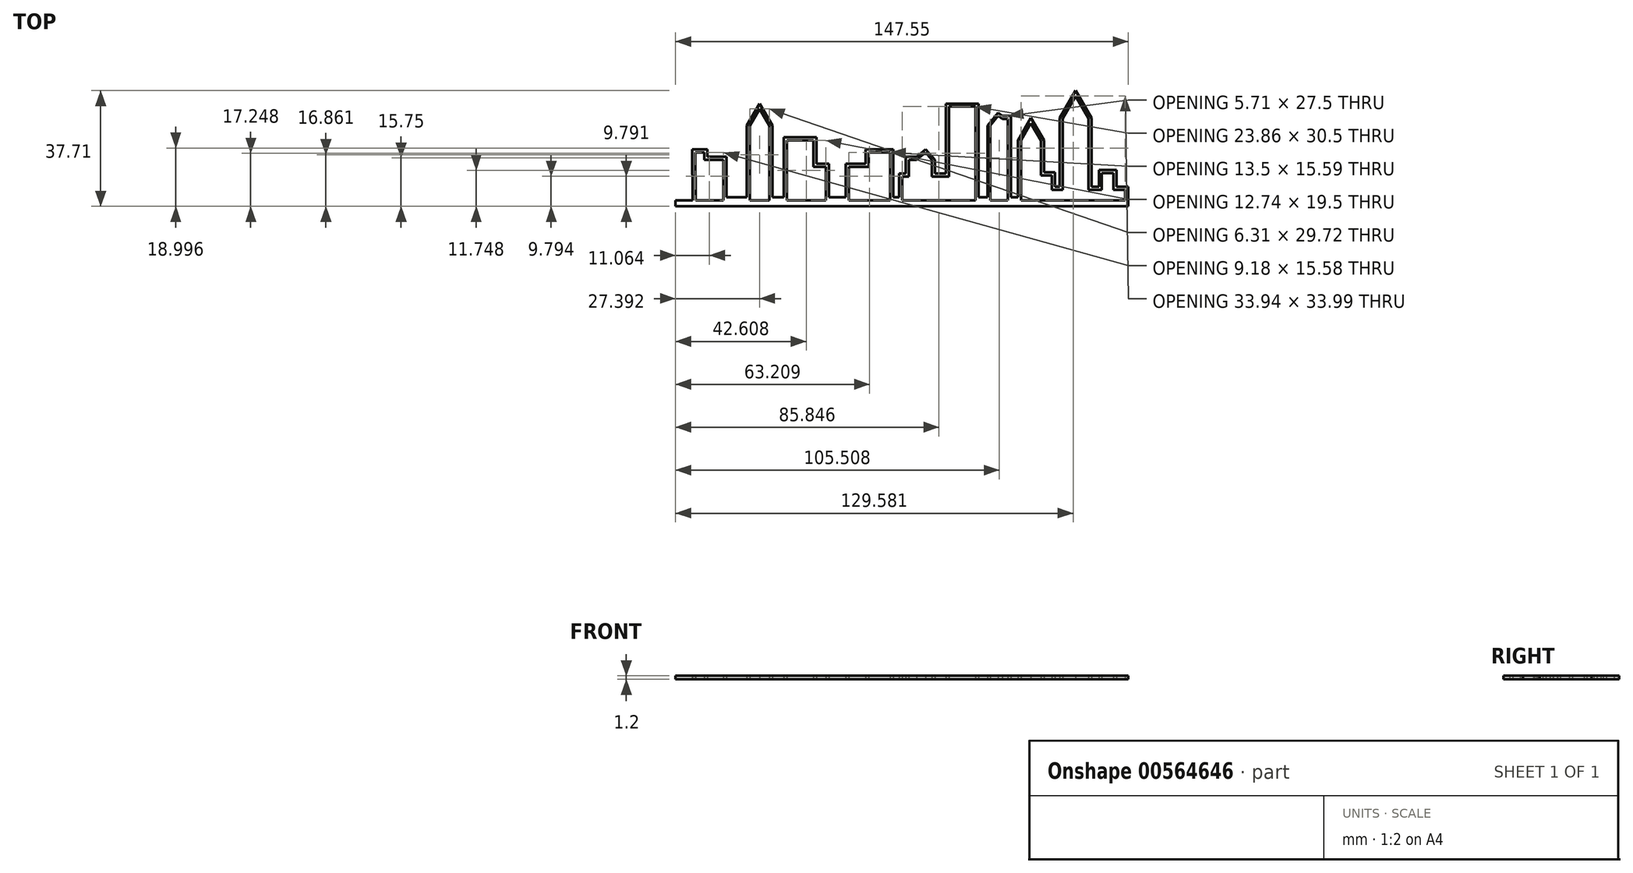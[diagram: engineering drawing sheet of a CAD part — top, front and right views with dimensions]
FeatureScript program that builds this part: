
annotation { "Feature Type Name" : "Feature", "Feature Type Description" : "" }
export const myFeature = defineFeature(function(context is Context, id is Id, definition is map)
    precondition{}
    {
        {
            var Q0;
            Q0=qCreatedBy(makeId("Top.planeOp"),FACE);
            var sketch = newSketch(context, id + "F0", { "sketchPlane" : qUnion([Q0])});
            skLineSegment(sketch, "E0", {"start": v(-8.8, 15.59) * mm, "end": v(-8.8, 10.82) * mm});
            skLineSegment(sketch, "E1", {"start": v(-8.8, 10.82) * mm, "end": v(-15.3, 10.82) * mm});
            skLineSegment(sketch, "E2", {"start": v(-15.3, 10.82) * mm, "end": v(-15.3, 1) * mm});
            skLineSegment(sketch, "E3", {"start": v(-17.9, 0) * mm, "end": v(-22.77, 0) * mm});
            skLineSegment(sketch, "E4", {"start": v(-22.77, 0) * mm, "end": v(-22.77, 10.82) * mm});
            skLineSegment(sketch, "E5", {"start": v(-26.82, 10.82) * mm, "end": v(-22.77, 10.82) * mm});
            skLineSegment(sketch, "E6", {"start": v(-26.82, 10.82) * mm, "end": v(-26.82, 19.5) * mm});
            skLineSegment(sketch, "E7", {"start": v(-26.82, 19.5) * mm, "end": v(-35.51, 19.5) * mm});
            skLineSegment(sketch, "E8", {"start": v(-35.51, 19.5) * mm, "end": v(-35.51, 0) * mm});
            skLineSegment(sketch, "E9", {"start": v(-35.51, 0) * mm, "end": v(-41.2, 0) * mm});
            skLineSegment(sketch, "E10", {"start": v(-41.2, 0) * mm, "end": v(-41.2, 24.26) * mm});
            skLineSegment(sketch, "E11", {"start": v(-41.2, 24.26) * mm, "end": v(-44.36, 29.72) * mm});
            skLineSegment(sketch, "E12", {"start": v(-47.51, 0) * mm, "end": v(-51.85, 0) * mm});
            skLineSegment(sketch, "E13", {"start": v(0, 0) * mm, "end": v(2.17, 0) * mm});
            skLineSegment(sketch, "E14", {"start": v(2.17, 0) * mm, "end": v(2.17, 7.73) * mm});
            skLineSegment(sketch, "E15", {"start": v(2.17, 7.73) * mm, "end": v(4.34, 7.73) * mm});
            skLineSegment(sketch, "E16", {"start": v(4.34, 7.73) * mm, "end": v(4.34, 13.15) * mm});
            skLineSegment(sketch, "E17", {"start": v(4.34, 13.15) * mm, "end": v(6.78, 13.15) * mm});
            skLineSegment(sketch, "E18", {"start": v(6.78, 13.15) * mm, "end": v(9.76, 15.59) * mm});
            skLineSegment(sketch, "E19", {"start": v(9.76, 15.59) * mm, "end": v(11.76, 13.15) * mm});
            skLineSegment(sketch, "E20", {"start": v(11.76, 13.15) * mm, "end": v(11.76, 7.73) * mm});
            skLineSegment(sketch, "E21", {"start": v(11.76, 7.73) * mm, "end": v(17.35, 7.73) * mm});
            skLineSegment(sketch, "E22", {"start": v(17.35, 7.73) * mm, "end": v(17.35, 30.5) * mm});
            skLineSegment(sketch, "E23", {"start": v(17.35, 30.5) * mm, "end": v(26.02, 30.5) * mm});
            skLineSegment(sketch, "E24", {"start": v(26.02, 30.5) * mm, "end": v(26.02, 7.73) * mm});
            skLineSegment(sketch, "E25", {"start": v(26.02, 7.73) * mm, "end": v(26.02, 0) * mm});
            skLineSegment(sketch, "E26", {"start": v(26.02, 0) * mm, "end": v(30.9, 0) * mm});
            skLineSegment(sketch, "E27", {"start": v(30.9, 0) * mm, "end": v(30.9, 19.5) * mm});
            skLineSegment(sketch, "E28", {"start": v(30.9, 19.5) * mm, "end": v(30.9, 24.26) * mm});
            skLineSegment(sketch, "E29", {"start": v(30.9, 24.26) * mm, "end": v(33.42, 27.5) * mm});
            skLineSegment(sketch, "E30", {"start": v(33.42, 27.5) * mm, "end": v(34.76, 26.45) * mm});
            skLineSegment(sketch, "E31", {"start": v(34.76, 26.45) * mm, "end": v(36.61, 26.45) * mm});
            skLineSegment(sketch, "E32", {"start": v(36.61, 26.45) * mm, "end": v(36.61, 24.26) * mm});
            skLineSegment(sketch, "E33", {"start": v(36.61, 24.26) * mm, "end": v(36.61, 0) * mm});
            skLineSegment(sketch, "E34", {"start": v(44.1, 25.12) * mm, "end": v(47.36, 19.5) * mm});
            skLineSegment(sketch, "E35", {"start": v(47.36, 19.5) * mm, "end": v(47.36, 8.1) * mm});
            skLineSegment(sketch, "E36", {"start": v(47.36, 8.1) * mm, "end": v(50.96, 8.1) * mm});
            skLineSegment(sketch, "E37", {"start": v(50.96, 8.1) * mm, "end": v(50.96, 3.39) * mm});
            skLineSegment(sketch, "E38", {"start": v(50.96, 3.39) * mm, "end": v(54.48, 3.39) * mm});
            skLineSegment(sketch, "E39", {"start": v(58.69, 34) * mm, "end": v(62.89, 26.71) * mm});
            skLineSegment(sketch, "E40", {"start": v(67.21, 3.39) * mm, "end": v(67.21, 8.81) * mm});
            skLineSegment(sketch, "E41", {"start": v(67.21, 8.81) * mm, "end": v(71, 8.81) * mm});
            skPoint(sketch, "E42.start.orphan", {"position": v(-66.14, 14.37) * mm});
            skLineSegment(sketch, "E43", {"start": v(-71.73, -2) * mm, "end": v(74.8, -2) * mm});
            skLineSegment(sketch, "E44", {"start": v(-66.14, 0) * mm, "end": v(74.8, 0) * mm});
            skLineSegment(sketch, "E45", {"start": v(74.8, 3.39) * mm, "end": v(74.8, 0) * mm});
            skPoint(sketch, "E46.orphan", {"position": v(76.22, -2) * mm});
            skLineSegment(sketch, "E47", {"start": v(74.8, -2) * mm, "end": v(75.8, -2) * mm});
            skLineSegment(sketch, "E48", {"start": v(75.8, -2) * mm, "end": v(75.8, 4.39) * mm});
            skPoint(sketch, "E49.start.orphan", {"position": v(72.9, 3.39) * mm});
            skLineSegment(sketch, "E50", {"start": v(74.8, 4.39) * mm, "end": v(72, 4.39) * mm});
            skLineSegment(sketch, "E51", {"start": v(72, 4.39) * mm, "end": v(72, 9.81) * mm});
            skLineSegment(sketch, "E52", {"start": v(68.57, 9.81) * mm, "end": v(72, 9.81) * mm});
            skLineSegment(sketch, "E53", {"start": v(74.8, 0) * mm, "end": v(75.8, 0) * mm});
            skLineSegment(sketch, "E54", {"start": v(66.21, 6.69) * mm, "end": v(66.21, 9.81) * mm});
            skLineSegment(sketch, "E55", {"start": v(68.57, 9.81) * mm, "end": v(66.21, 9.81) * mm});
            skLineSegment(sketch, "E56", {"start": v(66.21, 6.69) * mm, "end": v(66.21, 4.39) * mm});
            skLineSegment(sketch, "E57", {"start": v(64.7, 4.39) * mm, "end": v(66.21, 4.39) * mm});
            skLineSegment(sketch, "E58", {"start": v(64.7, 4.39) * mm, "end": v(63.88, 4.39) * mm});
            skLineSegment(sketch, "E59", {"start": v(54.48, 3.39) * mm, "end": v(54.48, 26.71) * mm});
            skLineSegment(sketch, "E60", {"start": v(53.48, 26.68) * mm, "end": v(53.48, 4.39) * mm});
            skLineSegment(sketch, "E61", {"start": v(53.48, 4.39) * mm, "end": v(51.96, 4.39) * mm});
            skLineSegment(sketch, "E62", {"start": v(51.96, 4.39) * mm, "end": v(51.96, 9.1) * mm});
            skLineSegment(sketch, "E63", {"start": v(51.96, 9.1) * mm, "end": v(48.36, 9.1) * mm});
            skPoint(sketch, "E64.start.orphan", {"position": v(39.32, 19.5) * mm});
            skLineSegment(sketch, "E65", {"start": v(54.48, 3.39) * mm, "end": v(74.8, 3.39) * mm});
            skLineSegment(sketch, "E66", {"start": v(71, 8.81) * mm, "end": v(71, 3.39) * mm});
            skPoint(sketch, "E67.orphan", {"position": v(71, 3.39) * mm});
            skPoint(sketch, "E68.orphan", {"position": v(74.8, 3.39) * mm});
            skPoint(sketch, "E69.end.orphan", {"position": v(62.88, 3.39) * mm});
            skLineSegment(sketch, "E70", {"start": v(62.89, 26.71) * mm, "end": v(62.89, 3.39) * mm});
            skLineSegment(sketch, "E71", {"start": v(62.89, 26.71) * mm, "end": v(54.48, 26.71) * mm});
            skLineSegment(sketch, "E72", {"start": v(54.48, 26.71) * mm, "end": v(58.69, 34) * mm});
            skLineSegment(sketch, "E73", {"start": v(63.89, 26.71) * mm, "end": v(63.88, 4.39) * mm});
            skLineSegment(sketch, "E74", {"start": v(63.89, 26.71) * mm, "end": v(58.7, 35.7) * mm});
            skLineSegment(sketch, "E75", {"start": v(53.48, 26.68) * mm, "end": v(58.7, 35.7) * mm});
            skLineSegment(sketch, "E76", {"start": v(48.36, 19.5) * mm, "end": v(48.36, 9.1) * mm});
            skLineSegment(sketch, "E77", {"start": v(48.36, 19.5) * mm, "end": v(44.1, 26.86) * mm});
            skLineSegment(sketch, "E78", {"start": v(37.61, 1) * mm, "end": v(37.61, 27.45) * mm});
            skLineSegment(sketch, "E79", {"start": v(34.76, 27.45) * mm, "end": v(37.61, 27.45) * mm});
            skLineSegment(sketch, "E80", {"start": v(34.23, 27.87) * mm, "end": v(34.41, 28.1) * mm});
            skLineSegment(sketch, "E81", {"start": v(34.76, 27.45) * mm, "end": v(33.42, 28.5) * mm});
            skLineSegment(sketch, "E82", {"start": v(33.42, 28.5) * mm, "end": v(29.9, 24.26) * mm});
            skLineSegment(sketch, "E83", {"start": v(29.9, 24.26) * mm, "end": v(29.9, 1) * mm});
            skPoint(sketch, "E84.start.orphan", {"position": v(28.46, 0) * mm});
            skLineSegment(sketch, "E85", {"start": v(29.9, 1) * mm, "end": v(27.02, 1) * mm});
            skLineSegment(sketch, "E86", {"start": v(27.02, 1) * mm, "end": v(27.02, 31.5) * mm});
            skPoint(sketch, "E87.start.orphan", {"position": v(21.69, 30.5) * mm});
            skLineSegment(sketch, "E88", {"start": v(27.02, 31.5) * mm, "end": v(16.35, 31.5) * mm});
            skLineSegment(sketch, "E89", {"start": v(16.35, 31.5) * mm, "end": v(16.35, 8.73) * mm});
            skPoint(sketch, "E90.start.orphan", {"position": v(14.55, 7.73) * mm});
            skLineSegment(sketch, "E91", {"start": v(16.35, 8.73) * mm, "end": v(12.76, 8.73) * mm});
            skLineSegment(sketch, "E92", {"start": v(12.76, 8.73) * mm, "end": v(12.76, 13.15) * mm});
            skLineSegment(sketch, "E93", {"start": v(4.34, 14.15) * mm, "end": v(6.78, 14.15) * mm});
            skLineSegment(sketch, "E94", {"start": v(6.78, 14.15) * mm, "end": v(9.76, 16.59) * mm});
            skLineSegment(sketch, "E95", {"start": v(12.76, 13.15) * mm, "end": v(9.76, 16.59) * mm});
            skLineSegment(sketch, "E96", {"start": v(4.34, 14.15) * mm, "end": v(3.34, 14.15) * mm});
            skLineSegment(sketch, "E97", {"start": v(3.34, 14.15) * mm, "end": v(3.34, 8.73) * mm});
            skLineSegment(sketch, "E98", {"start": v(-8.8, 15.59) * mm, "end": v(-1.8, 15.59) * mm});
            skLineSegment(sketch, "E99", {"start": v(-1.8, 15.59) * mm, "end": v(-1.8, 0) * mm});
            skLineSegment(sketch, "E100", {"start": v(3.34, 8.73) * mm, "end": v(1.17, 8.73) * mm});
            skLineSegment(sketch, "E101", {"start": v(1.17, 8.73) * mm, "end": v(1.17, 1) * mm});
            skLineSegment(sketch, "E102", {"start": v(1.17, 1) * mm, "end": v(-0.8, 1) * mm});
            skLineSegment(sketch, "E103", {"start": v(-0.8, 1) * mm, "end": v(-0.8, 16.59) * mm});
            skLineSegment(sketch, "E104", {"start": v(-0.8, 16.59) * mm, "end": v(-9.8, 16.59) * mm});
            skLineSegment(sketch, "E105", {"start": v(-9.8, 16.59) * mm, "end": v(-9.8, 11.82) * mm});
            skLineSegment(sketch, "E106", {"start": v(-9.8, 11.82) * mm, "end": v(-16.3, 11.82) * mm});
            skPoint(sketch, "E107.start.orphan", {"position": v(-20.33, 0) * mm});
            skLineSegment(sketch, "E108", {"start": v(-21.77, 1) * mm, "end": v(-21.77, 11.82) * mm});
            skLineSegment(sketch, "E109", {"start": v(-21.77, 11.82) * mm, "end": v(-25.82, 11.82) * mm});
            skLineSegment(sketch, "E110", {"start": v(-25.82, 11.82) * mm, "end": v(-25.82, 20.5) * mm});
            skLineSegment(sketch, "E111", {"start": v(-30.47, 20.5) * mm, "end": v(-25.82, 20.5) * mm});
            skLineSegment(sketch, "E112", {"start": v(-30.47, 20.5) * mm, "end": v(-36.51, 20.5) * mm});
            skPoint(sketch, "E113.start.orphan", {"position": v(-26.82, 15.16) * mm});
            skLineSegment(sketch, "E114", {"start": v(-36.51, 20.5) * mm, "end": v(-36.51, 1) * mm});
            skLineSegment(sketch, "E115", {"start": v(-36.51, 1) * mm, "end": v(-40.2, 1) * mm});
            skLineSegment(sketch, "E116", {"start": v(-40.2, 1) * mm, "end": v(-40.2, 24.26) * mm});
            skLineSegment(sketch, "E117", {"start": v(-41.2, 24.26) * mm, "end": v(-47.51, 24.26) * mm});
            skPoint(sketch, "E118.start.orphan", {"position": v(-47.51, 24.26) * mm});
            skPoint(sketch, "E119.end.orphan", {"position": v(-50.96, 1) * mm});
            skLineSegment(sketch, "E120", {"start": v(-47.51, 0) * mm, "end": v(-47.51, 24.26) * mm});
            skLineSegment(sketch, "E121", {"start": v(-47.51, 24.26) * mm, "end": v(-44.36, 29.72) * mm});
            skLineSegment(sketch, "E122", {"start": v(-48.51, 24.26) * mm, "end": v(-44.36, 31.45) * mm});
            skLineSegment(sketch, "E123", {"start": v(-40.2, 24.26) * mm, "end": v(-44.36, 31.45) * mm});
            skLineSegment(sketch, "E124", {"start": v(-48.51, 24.26) * mm, "end": v(-48.51, 1) * mm});
            skPoint(sketch, "E125.end.orphan", {"position": v(-55.1, 0) * mm});
            skPoint(sketch, "E126.orphan", {"position": v(-55.1, 1) * mm});
            skLineSegment(sketch, "E127", {"start": v(-16.3, 11.82) * mm, "end": v(-16.3, 1) * mm});
            skLineSegment(sketch, "E128", {"start": v(-21.77, 1) * mm, "end": v(-16.3, 1) * mm});
            skLineSegment(sketch, "E129", {"start": v(-15.3, 1) * mm, "end": v(-15.3, 0) * mm});
            skLineSegment(sketch, "E130", {"start": v(74.8, 4.39) * mm, "end": v(75.8, 4.39) * mm});
            skLineSegment(sketch, "E131", {"start": v(47.36, 19.5) * mm, "end": v(40.86, 19.5) * mm});
            skLineSegment(sketch, "E132", {"start": v(40.86, 19.5) * mm, "end": v(44.1, 25.12) * mm});
            skPoint(sketch, "E133.orphan", {"position": v(43.34, 26.45) * mm});
            skLineSegment(sketch, "E134", {"start": v(39.86, 19.5) * mm, "end": v(44.1, 26.86) * mm});
            skLineSegment(sketch, "E135", {"start": v(39.86, 19.5) * mm, "end": v(39.86, 1) * mm});
            skLineSegment(sketch, "E136", {"start": v(40.86, 19.5) * mm, "end": v(40.86, 0) * mm});
            skLineSegment(sketch, "E137", {"start": v(37.61, 1) * mm, "end": v(39.86, 1) * mm});
            skLineSegment(sketch, "E138", {"start": v(-48.51, 1) * mm, "end": v(-55.1, 1) * mm});
            skLineSegment(sketch, "E139", {"start": v(-55.1, 1) * mm, "end": v(-55.1, 14.2) * mm});
            skLineSegment(sketch, "E140", {"start": v(-55.1, 14.2) * mm, "end": v(-61.35, 14.2) * mm});
            skLineSegment(sketch, "E141", {"start": v(-61.35, 14.2) * mm, "end": v(-61.35, 16.56) * mm});
            skLineSegment(sketch, "E142", {"start": v(-61.35, 16.56) * mm, "end": v(-66.28, 16.56) * mm});
            skPoint(sketch, "E143.end.orphan", {"position": v(-66.14, 15.59) * mm});
            skPoint(sketch, "E144.end.orphan", {"position": v(-66.14, 13.15) * mm});
            skLineSegment(sketch, "E145", {"start": v(-66.28, 16.56) * mm, "end": v(-66.14, 0) * mm});
            skLineSegment(sketch, "E146", {"start": v(-66.14, 0) * mm, "end": v(-71.75, -0.05) * mm});
            skLineSegment(sketch, "E147", {"start": v(-71.75, -0.05) * mm, "end": v(-71.73, -2) * mm});
            skPoint(sketch, "E148.start.orphan", {"position": v(-63.82, 16.56) * mm});
            skLineSegment(sketch, "E149", {"start": v(-65.28, 15.56) * mm, "end": v(-62.35, 15.58) * mm});
            skLineSegment(sketch, "E150", {"start": v(-62.35, 15.06) * mm, "end": v(-62.35, 15.58) * mm});
            skLineSegment(sketch, "E151", {"start": v(-62.35, 15.06) * mm, "end": v(-62.35, 13.2) * mm});
            skLineSegment(sketch, "E152", {"start": v(-62.35, 13.2) * mm, "end": v(-56.1, 13.2) * mm});
            skLineSegment(sketch, "E153", {"start": v(-65.28, 15.56) * mm, "end": v(-65.14, 0) * mm});
            skLineSegment(sketch, "E154", {"start": v(-56.1, 13.2) * mm, "end": v(-56.1, 0) * mm});
            skSolve(sketch);
        }
        {
            var Q0;
            Q0=qSketchRegion(id+"F0",true);
            extrude(context, id + "F1", {"entities" : qUnion([Q0]), "depth" : 1.2 * mm, "offsetDistance" : 25 * mm});
        }
    });
